# Revit family: Naava One
name_source: partatom
category: Furniture
revit_build: Autodesk Revit 2015 (Build: 20140223_1515(x64)
units: mm (PartAtom-declared; Revit-internal decimal feet)

## types (6) — shared parameters
Manufacturer = Naava
URL = www.naava.io
W6 = Yes

## per-type parameters (varying)
| type | Frame | Height | Plant Row | Planter Row | W10 | Width |
| N100x210 White | Naava White RAL9016 | 2091 mm  [stored 6.86024 ft] | 3 | 7 | Yes | 1000 mm  [stored 3.28084 ft] |
| N100x231 White | Naava White RAL9016 | 2301 mm | 4 | 8 | Yes | 1000 mm  [stored 3.28084 ft] |
| N60x210 White | Naava White RAL9016 | 2091 mm  [stored 6.86024 ft] | 3 | 7 | No | 600 mm |
| N100x210 Black | Naava Graphite Black RAL9011 | 2091 mm  [stored 6.86024 ft] | 3 | 7 | Yes | 1000 mm  [stored 3.28084 ft] |
| N100x231 Black | Naava Graphite Black RAL9011 | 2301 mm | 4 | 8 | Yes | 1000 mm  [stored 3.28084 ft] |
| N60x210 Black | Naava Graphite Black RAL9011 | 2091 mm  [stored 6.86024 ft] | 3 | 7 | No | 600 mm |

note: [stored X ft] marks values corroborated as IEEE doubles in the binary element streams (Revit-internal decimal feet)

## geometry (parser evidence)
native form markers: Sweep x14
no freeform markers — native parametric forms only
